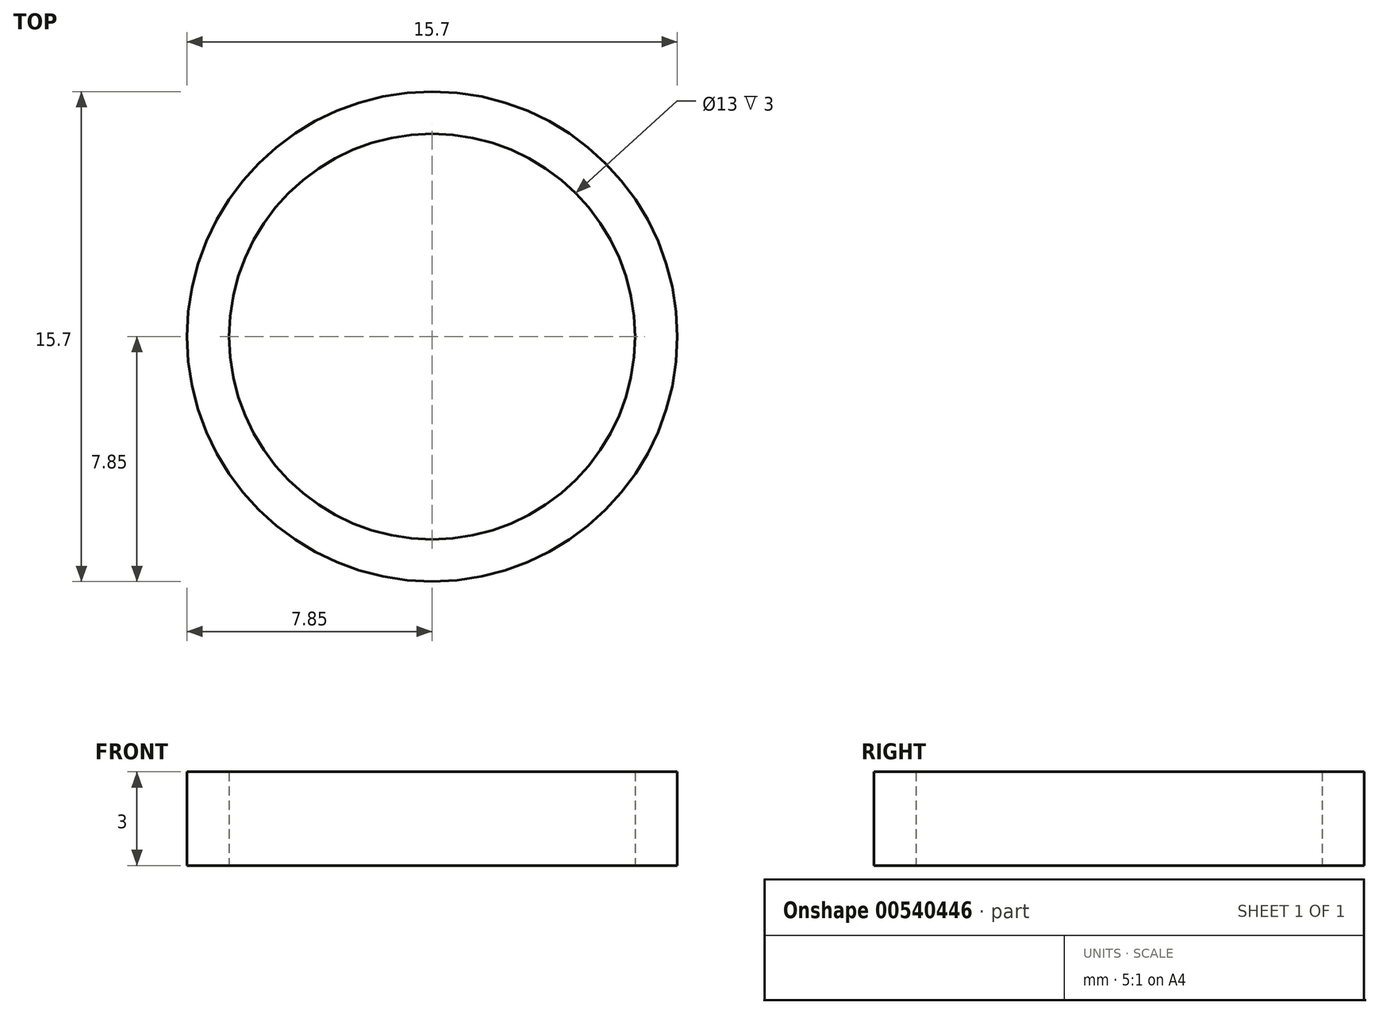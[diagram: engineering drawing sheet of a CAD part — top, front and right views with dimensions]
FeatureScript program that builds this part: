
annotation { "Feature Type Name" : "Feature", "Feature Type Description" : "" }
export const myFeature = defineFeature(function(context is Context, id is Id, definition is map)
    precondition{}
    {
        {
            var Q0;
            Q0=qCreatedBy(makeId("Top.planeOp"),FACE);
            var sketch = newSketch(context, id + "F0", { "sketchPlane" : qUnion([Q0])});
            skCircle(sketch, "E0", {"center": v(0, 0) * mm, "radius": 7.85 * mm});
            skCircle(sketch, "E1", {"center": v(0, 0) * mm, "radius": 6.5 * mm});
            skSolve(sketch);
        }
        {
            var Q0;
            Q0=makeQuery(id+"F0.imprint","IMPRINT",FACE,{"disambiguationData":[TD([[makeQuery(id+"F0.imprint","IMPRINT",EDGE,{"derivedFrom":sQuery(id+"F0.wireOp",EDGE,"E0")}),1.0]])]});
            extrude(context, id + "F1", {"entities" : qUnion([Q0]), "depth" : 3 * mm, "offsetDistance" : 25 * mm});
        }
    });
